# Revit family: Thermostatic_Mixing_Valve-Lead_Free-MGI_Controls-Alpha-STP7069-12S_Series
name_source: partatom
category: Pipe Accessories
units: mm (PartAtom-declared; Revit-internal decimal feet)

## family parameters
Always vertical = No
Cut with Voids When Loaded = No
OmniClass Number = 23.65.55.14
OmniClass Title = Valves for Liquid Services
Part Type = Valve - Breaks Into
Round Connector Dimension = Use Diameter
Shared = Yes
Work Plane-Based = Yes

## types (8) — shared parameters
Assembly Code = D2090900
CW Connection = Yes
Cold Water Connection Description = 1/2” CW NPS Inlet
Cold Water Connection Diameter = 1/2"
Default Elevation = 0"
Description = Lead-Free Tempering Valve
Dual-Function Thermostatic Cartridge Valve Type = Yes
Finish = Plastic-Delta-Black
Finish- Others = Brass-Delta-Satin
HW Connection = Yes
Height = 3 3/8"
Hot Water Connection Description = 1/2” HW NPS Inlet
Hot Water Connection Diameter = 1"
IAPMO Compliance = IAPMO certified to ASSE 1070, ASSE 1069
Installation Instruction Link = https://www.mgicontrols.com
Manufacturer = MGI Controls
Material = Plastic-Delta-Black
Max. Working Pressure = 145 psi (1,000 kPa)
Price = Prices may vary. Please consult Manufacturer Representative for most up-to-date price list.
Product Documentation Link = https://www.mgicontrols.com
Product Page URL = https://www.mgicontrols.com
Temperature Range = 85°F-115°F (29°C-46°C)
Tempered Water Connection = Yes
Tempered Water Connection Description = 1/2” NPS Tempered Water Inlet
Tempered Water Connection Diameter = 1/2"
Thermostatic Mixing Valve = Yes
URL = https://www.mgicontrols.com
Width = 3 1/4"

## per-type parameters (varying)
| type | Flow Rate | Pressure Drop PSID (kPa) |
| STP7069-12S- 0.7LPM | 7 LPM | Cv |
| STP7069-12S- 1.5LPM | 1.5 LPM | 5 |
| STP7069-12S- 2.1LPM | 2.1 LPM | 10 |
| STP7069-12S- 2.6LPM | 2.6 LPM | 15 |
| STP7069-12S- 3LPM | 3 LPM | 20 |
| STP7069-12S- 3.7LPM | 3.7 LPM | 30 |
| STP7069-12S- 4.5LPM | 4.5 LPM | 45 |
| STP7069-12S- 5.2LPM | 5.2 LPM | 60 |

note: column(s) folded — value = type name in every type: Model

## geometry (parser evidence)
native form markers: Sweep x3
no freeform markers — native parametric forms only
